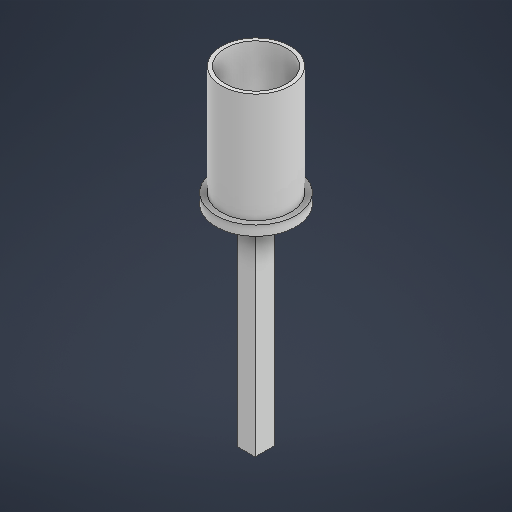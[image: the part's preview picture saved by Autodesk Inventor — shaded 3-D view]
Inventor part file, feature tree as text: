
AUTODESK INVENTOR PART (.ipt)
format: ipt  version: 2025 (Build 290162000, 162)  size: 277,504 bytes
history: native  units: in
note: dims shown in document units (in); Inventor stores cm internally (conversion verified against a paired STEP export)
features: extrude x9, sketch x5
ambient origin geometry x8: Origin, YZ Plane, XZ Plane, XY Plane, X Axis, Y Axis, Z Axis, Center Point
bodies: Solid1 (feature_tree)
feature tree (14):
  sketch  "Sketch1"  dims[d0=8.6614in d1=7.4803in]
  extrude  "Extrusion1"  Depth=7.4803in
  extrude  "Extrusion2"  Depth=1.063in TaperAngle=0.0deg
  extrude  "Extrusion3"  Depth=11.811in TaperAngle=0.0deg
  sketch  "Sketch3"  dims[d6=6.6929in d7=11.811in d8=0.0in]
  extrude  "Extrusion4"  Depth=2.5984in
  extrude  "Extrusion5"  Depth=2.1654in
  extrude  "Extrusion6"  Depth=0.3937in
  extrude  "Extrusion7"  Depth=0.9843in TaperAngle=0.0deg
  sketch  "Sketch5"  dims[d11=1.9685in d12=2.1654in d13=3.937in d14=0.9843in d15=0.0in d16=22.8346in d17=0.0in d18=1.1811in d19=0.0in d20=0.0787in d21=0.0in d22=0.0in d23=2.5591in d24=1.75in d25=0.1772in d26=0.1772in d27=0.1772in d28=0.1772in d29=1.1811in d30=0.3937in d31=0.0in d32=0.0in d33=0.0in]
  extrude  "Extrusion8"  Depth=22.8346in TaperAngle=0.0deg
  extrude  "Extrusion9"  Depth=1.1811in TaperAngle=0.0deg
  sketch  "Sketch2"  dims[d2=12.9921in d3=0.0in d4=1.063in d5=0.0in]
  sketch  "Sketch4"  dims[d9=2.8346in d10=2.5984in]
